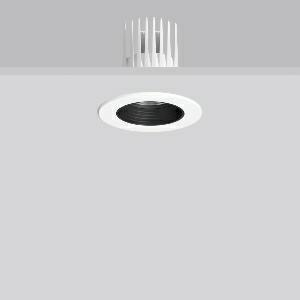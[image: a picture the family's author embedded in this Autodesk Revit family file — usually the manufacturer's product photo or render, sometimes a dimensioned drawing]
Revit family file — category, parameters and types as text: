
# Revit family: heledon_mini_e_901753_002_46d1
name_source: partatom
category: Lighting Fixtures
units: mm (PartAtom-declared; Revit-internal decimal feet)

## family parameters
Cut with Voids When Loaded = No
Host = Face
Light Source = No
Part Type = Normal
Room Calculation Point = No
Round Connector Dimension = Use Diameter
Shared = No

## types (1)
- HELEDON mini E (1 x LED Modul 930, 2850 lm, 3000)
    Apparent Load = 29 VA
    Approval mark = CE
    CIE Flux Codes = 98 100 100 100 100
    Color Rendering = 90
    Color Temperature = 3000
    Default Elevation = 1800 mm
    Description = Series: HELEDON mini
Round recessed downlight. Housing: die-cast aluminium, powder-coated. Black plastic ring and recessed LED to prevent glare from the side. Optical assembly with lens made of plastic (polycarbonate) for the best homogeneous light distribution - can be changed without tools. Best colour rendering index Ra>90. Suitable for Recessed ceiling mounting. Installation without tools thanks to spring fastening system. Including separate LED converter with connecting cable 600 mm.High quality converter without flickering and stroboscopic effect. Through-wiring box (5 pole) available as accessory. The following accessories can be mounted without use of tools: interchangeable lenses, decorative glasses, honeycomb louvre, clear and frosted diffusers, white interchangeable plastic ring. 
Colour: traffic white, matt (RAL 9016)
Diameter: 124 mm
Height: 3 mm
Cut-out diameter: 114 mm
Recess height: 170 mm
Luminaire: recess height: 120 mm
Lamp: LED
Socket: without socket
Colour temperature: 3000K
Colour rendering index (CRI): 92
System power: 29 W
Rated luminous flux: 2850 lm
Luminous efficiency: 98 lm/W
Control gear: Regulated power supply
Protection class: II
Type of protection: IP 20
    Height = 0 mm  [stored 0 ft]
    Lamp = 1 x LED Modul 930
    Lamp Light Flux = 2850 lm
    Lamp count = 1
    Length = 124 mm  [stored 0.406824 ft]
    Lifetime = 50000 h
    Luminous efficacy = 98 lm/W
    Manufacturer = RZB
    ModVariant = No
    Model = 901753.002
    Mounting Place = Ceiling
    Mounting Type = Recessed
    Number of Poles = 1
    OnlyDefault = Yes
    Power Factor = 1
    Product Name = HELEDON mini E
    Product group = Recessed downlights
    ProductGroupID = 402
    Protection Class = Protection class II
    Protection Degree = IP 20
    RLX_Detail_Level = 1
    RLX_Emergency_Light_Flux = 0 lm
    RLX_Emergency_Type = 0
    RLX_Emergency_Type_DB = No
    RlxData = <blob elided: 126693 chars, md5=6cb98cf0>
    Socket = socket
    Standby Power = 0 W
    System Light Flux = 2850 lm
    System Power = 29 W
    Type Comments = Product without accessories
    Type Image = 901656.002.jpg
    URL = http://relux.com
    VarID = ---
    Voltage = 230 V
    Voltage Range = 220-240 V
    Weight = 0.00 kg
    Width = 0 mm  [stored 0 ft]

note: [stored X ft] marks values corroborated as IEEE doubles in the binary element streams (Revit-internal decimal feet)

## geometry (parser evidence)
native form markers: Blend x4, Sweep x11
no freeform markers — native parametric forms only
